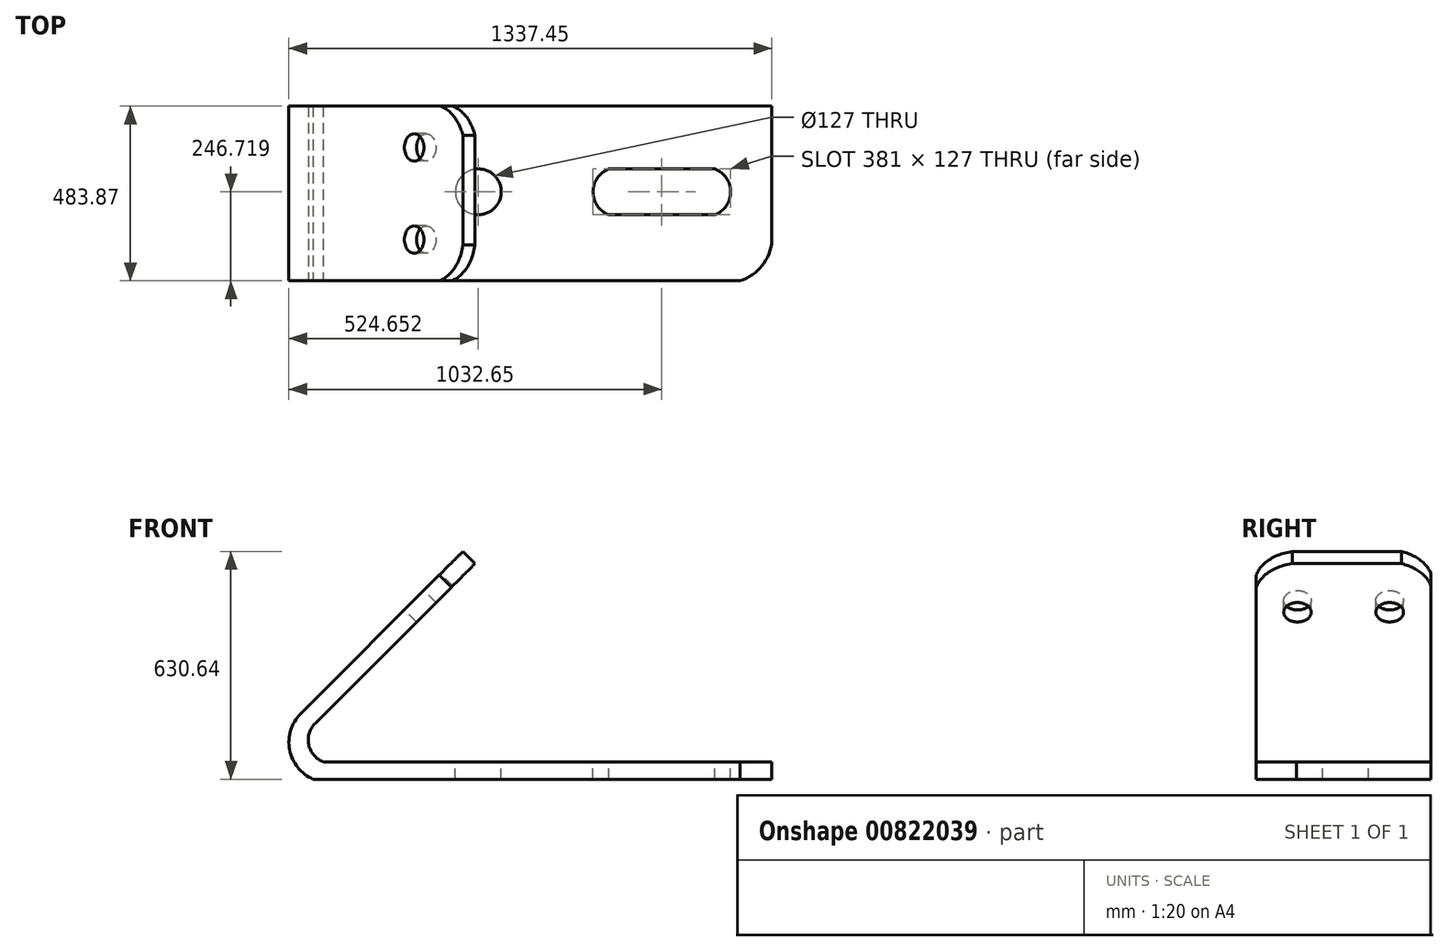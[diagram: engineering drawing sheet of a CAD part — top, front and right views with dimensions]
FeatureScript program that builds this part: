
annotation { "Feature Type Name" : "Feature", "Feature Type Description" : "" }
export const myFeature = defineFeature(function(context is Context, id is Id, definition is map)
    precondition{}
    {
        {
            var Q0;
            Q0=qCreatedBy(makeId("Front.planeOp"),FACE);
            var sketch = newSketch(context, id + "F0", { "sketchPlane" : qUnion([Q0])});
            skLineSegment(sketch, "E0", {"start": v(769.31, -350.95) * mm, "end": v(769.31, -399.21) * mm});
            skLineSegment(sketch, "E1", {"start": v(769.31, -399.21) * mm, "end": v(-500.69, -399.21) * mm});
            skLineSegment(sketch, "E2", {"start": v(-495.39, -244.56) * mm, "end": v(-46.37, 204.45) * mm});
            skLineSegment(sketch, "E3", {"start": v(-46.37, 204.45) * mm, "end": v(-86.4, 231.43) * mm});
            skLineSegment(sketch, "E4", {"start": v(-86.4, 231.43) * mm, "end": v(-535.4, -217.59) * mm});
            skArc(sketch, "E5", {"start": v(-535.4, -217.59) * mm, "mid": v(-566.15, -317.6) * mm, "end": v(-500.69, -399.21) * mm});
            skLineSegment(sketch, "E6", {"start": v(769.31, -350.95) * mm, "end": v(-473.35, -350.95) * mm});
            skArc(sketch, "E7", {"start": v(-495.39, -244.56) * mm, "mid": v(-513.07, -303.7) * mm, "end": v(-473.35, -350.95) * mm});
            skSolve(sketch);
        }
        {
            var Q0;
            Q0=makeQuery(id+"F0.imprint","IMPRINT",FACE,{"disambiguationData":[TD([[makeQuery(id+"F0.imprint","IMPRINT",EDGE,{"derivedFrom":sQuery(id+"F0.wireOp",EDGE,"E0")}),-1.0]])]});
            extrude(context, id + "F1", {"entities" : qUnion([Q0]), "oppositeDirection" : true, "depth" : 483.87 * mm, "offsetDistance" : 25.4 * mm});
        }
        {
            var Q0;
            Q0=makeQuery(id+"F1.opExtrude","SWEPT_FACE",FACE,{"disambiguationData":[OSD([sQuery(id+"F0.wireOp",EDGE,"E6")])]});
            var sketch = newSketch(context, id + "F2", { "sketchPlane" : qUnion([Q0])});
            skLineSegment(sketch, "E8.bottom", {"start": v(611, 310.22) * mm, "end": v(318.01, 310.22) * mm});
            skLineSegment(sketch, "E8.top", {"start": v(611, 183.22) * mm, "end": v(318.01, 183.22) * mm});
            skLineSegment(sketch, "E8.left", {"start": v(611, 310.22) * mm, "end": v(611, 183.22) * mm});
            skLineSegment(sketch, "E8.right", {"start": v(318.01, 310.22) * mm, "end": v(318.01, 183.22) * mm});
            skArc(sketch, "E9", {"start": v(611, 183.22) * mm, "mid": v(655.01, 246.72) * mm, "end": v(611, 310.22) * mm});
            skArc(sketch, "E10", {"start": v(318.01, 310.22) * mm, "mid": v(274.01, 246.72) * mm, "end": v(318.01, 183.22) * mm});
            skCircle(sketch, "E11", {"center": v(-43.49, 246.72) * mm, "radius": 63.5 * mm});
            skArc(sketch, "E12", {"start": v(769.31, 389.01) * mm, "mid": v(723.53, 457.8) * mm, "end": v(645.1, 483.87) * mm});
            skArc(sketch, "E13", {"start": v(680.9, 0) * mm, "mid": v(742.03, 41.96) * mm, "end": v(769.31, 110.9) * mm});
            skSolve(sketch);
        }
        {
            var Q0;
            Q0=makeQuery(id+"F2.imprint","IMPRINT",FACE,{"disambiguationData":[TD([[makeQuery(id+"F2.imprint","IMPRINT",EDGE,{"derivedFrom":sQuery(id+"F2.wireOp",EDGE,"E11")}),1.0]])]});
            var Q1;
            Q1=makeQuery(id+"F2.imprint","IMPRINT",FACE,{"disambiguationData":[TD([[makeQuery(id+"F2.imprint","IMPRINT",EDGE,{"derivedFrom":sQuery(id+"F2.wireOp",EDGE,"E8.bottom")}),1.0]])]});
            var Q2;
            Q2=makeQuery(id+"F2.imprint","IMPRINT",FACE,{"disambiguationData":[TD([[makeQuery(id+"F2.imprint","IMPRINT",EDGE,{"derivedFrom":sQuery(id+"F2.wireOp",EDGE,"E8.left")}),1.0]])]});
            var Q3;
            Q3=makeQuery(id+"F2.imprint","IMPRINT",FACE,{"disambiguationData":[TD([[makeQuery(id+"F2.imprint","IMPRINT",EDGE,{"derivedFrom":sQuery(id+"F2.wireOp",EDGE,"E8.right")}),-1.0]])]});
            var Q4;
            {var subQ0=sQuery(id+"F2.wireOp",EDGE,"E12");var subQ1=sQuery(id+"F0.wireOp",EDGE,"E6");var subQ4=makeQuery(id+"F1.opExtrude","CAP_EDGE",EDGE,{"disambiguationData":[OSD([subQ1])],"isStart":false});var subQ5=makeQuery(id+"F2.imprint","INTERSECT",VERTEX,{"disambiguationData":[OD(1.0)],"derivedFrom":[subQ4,subQ0]});Q4=makeQuery(id+"F2.imprint","IMPRINT",FACE,{"disambiguationData":[TD([[makeQuery(id+"F2.imprint","IMPRINT",EDGE,{"disambiguationData":[TD([[subQ5,1.0]])],"derivedFrom":subQ0}),-1.0]])]});}
            var Q5;
            {var subQ0=sQuery(id+"F2.wireOp",EDGE,"E13");Q5=makeQuery(id+"F2.imprint","IMPRINT",FACE,{"disambiguationData":[TD([[makeQuery(id+"F2.imprint","IMPRINT",EDGE,{"derivedFrom":subQ0}),-1.0]])]});}
            extrude(context, id + "F3", {"entities" : qUnion([Q0, Q1, Q2, Q3, Q4, Q5]), "operationType" : NewBodyOperationType.REMOVE, "endBound" : BoundingType.THROUGH_ALL, "oppositeDirection" : true, "depth" : 25.4 * mm, "offsetDistance" : 25.4 * mm});
        }
        {
            var Q0;
            Q0=makeQuery(id+"F1.opExtrude","SWEPT_FACE",FACE,{"disambiguationData":[OSD([sQuery(id+"F0.wireOp",EDGE,"E4")])]});
            var sketch = newSketch(context, id + "F4", { "sketchPlane" : qUnion([Q0])});
            skCircle(sketch, "E14", {"center": v(-369.57, -87.95) * mm, "radius": 38.1 * mm});
            skCircle(sketch, "E15", {"center": v(-114.3, -87.95) * mm, "radius": 38.1 * mm});
            skArc(sketch, "E16", {"start": v(0, 10.4) * mm, "mid": v(-36.43, 70.88) * mm, "end": v(-99.54, 102.55) * mm});
            skArc(sketch, "E17", {"start": v(-402.85, 102.55) * mm, "mid": v(-454.06, 69.35) * mm, "end": v(-483.87, 16.09) * mm});
            skSolve(sketch);
        }
        {
            var Q0;
            Q0=makeQuery(id+"F4.imprint","IMPRINT",FACE,{"disambiguationData":[TD([[makeQuery(id+"F4.imprint","IMPRINT",EDGE,{"derivedFrom":sQuery(id+"F4.wireOp",EDGE,"E14")}),1.0]])]});
            var Q1;
            Q1=makeQuery(id+"F4.imprint","IMPRINT",FACE,{"disambiguationData":[TD([[makeQuery(id+"F4.imprint","IMPRINT",EDGE,{"derivedFrom":sQuery(id+"F4.wireOp",EDGE,"E15")}),1.0]])]});
            var Q2;
            {var subQ0=sQuery(id+"F4.wireOp",EDGE,"E16");Q2=makeQuery(id+"F4.imprint","IMPRINT",FACE,{"disambiguationData":[TD([[makeQuery(id+"F4.imprint","IMPRINT",EDGE,{"derivedFrom":subQ0}),-1.0]])]});}
            var Q3;
            {var subQ0=sQuery(id+"F4.wireOp",EDGE,"E17");Q3=makeQuery(id+"F4.imprint","IMPRINT",FACE,{"disambiguationData":[TD([[makeQuery(id+"F4.imprint","IMPRINT",EDGE,{"derivedFrom":subQ0}),-1.0]])]});}
            extrude(context, id + "F5", {"entities" : qUnion([Q0, Q1, Q2, Q3]), "operationType" : NewBodyOperationType.REMOVE, "oppositeDirection" : true, "depth" : 78.74 * mm, "offsetDistance" : 25.4 * mm});
        }
        {
            var Q0;
            {var subQ0=sQuery(id+"F0.wireOp",EDGE,"E2");var subQ1=sQuery(id+"F0.wireOp",EDGE,"E3");var subQ2=sQuery(id+"F0.wireOp",EDGE,"E4");Q0=makeQuery(id+"F5.boolean.opBoolean","SPLIT",FACE,{"disambiguationData":[TD([makeQuery(id+"F1.opExtrude","SWEPT_FACE",FACE,{"disambiguationData":[OSD([subQ1])]})])],"derivedFrom":makeQuery(id+"F1.opExtrude","CAP_FACE",FACE,{"disambiguationData":[OSD([sQuery(id+"F0.wireOp",EDGE,"E0"),sQuery(id+"F0.wireOp",EDGE,"E1"),subQ0,subQ1,subQ2,sQuery(id+"F0.wireOp",EDGE,"E5"),sQuery(id+"F0.wireOp",EDGE,"E6"),sQuery(id+"F0.wireOp",EDGE,"E7")])],"isStart":true})});}
            extrude(context, id + "F6", {"entities" : qUnion([Q0]), "operationType" : NewBodyOperationType.REMOVE, "endBound" : BoundingType.THROUGH_ALL, "oppositeDirection" : true, "depth" : 25.4 * mm, "offsetDistance" : 25.4 * mm});
        }
    });
